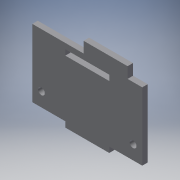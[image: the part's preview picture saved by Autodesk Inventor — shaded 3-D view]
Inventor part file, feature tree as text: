
AUTODESK INVENTOR PART (.ipt)
format: ipt  version: 2018 (Build 220112000, 112)  size: 130,560 bytes
history: native  units: in
note: dims shown in document units (in); Inventor stores cm internally (conversion verified against a paired STEP export)
features: reference x12, other x6, extrude x3, sketch x3
ambient origin geometry x8: Origin, YZ Plane, XZ Plane, XY Plane, X Axis, Y Axis, Z Axis, Center Point
bodies: Solid1 (feature_tree)
feature tree (24):
  extrude  "Extrusion1"  Depth=0.315in
  extrude  "Extrusion2"  Depth=0.2362in
  extrude  "Extrusion3"  Depth=0.1181in
  sketch  "Sketch1"  dims[d0=1.5748in d1=0.315in]
  reference  "Reference1"
  reference  "Reference2"
  reference  "Reference3"
  reference  "Reference4"
  reference  "Reference5"
  reference  "Reference6"
  reference  "Reference7"
  reference  "Reference8"
  sketch  "Sketch2"  dims[d2=0.9449in d3=0.2362in]
  reference  "Reference9"
  reference  "Reference10"
  sketch  "Sketch3"  dims[d4=0.1181in d5=0.1181in d6=0.9449in d7=0.1181in d8=0.0in d9=0.1181in d10=0.0in d11=0.8819in d12=0.0in]
  reference  "Reference11"
  reference  "Reference12"
  other  "Camera pan and tilt assembly.iam"
  other  "Camera pan base:1"
  other  "Servo motor:3"
  other  "Servo body:1"
  other  "Angle bracket short:8"
  other  "Angle bracket short:7"
